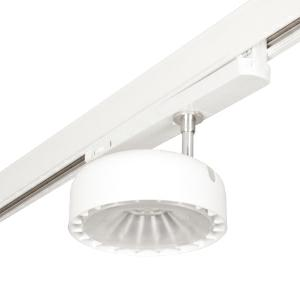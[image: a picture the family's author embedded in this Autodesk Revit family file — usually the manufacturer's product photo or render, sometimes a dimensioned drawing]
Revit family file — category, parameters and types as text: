
# Revit family: 3f_filippi_-_3f_emilio_track_ellittico_3f_filippi_-_47608_-_3f_emilio_tk_led_4000-840_ell
name_source: partatom
category: Lighting Fixtures
units: mm (PartAtom-declared; Revit-internal decimal feet)

## family parameters
Cut with Voids When Loaded = No
Host = Face
Light Source = No
Part Type = Normal
Room Calculation Point = No
Round Connector Dimension = Use Diameter
Shared = No

## types (1)
- 3F Filippi - 3F Emilio Track Ellittico (1 x LED, 4086 lm, 34 W, 4000 K)
    Apparent Load = 34 VA
    Approval mark = CE
    CIE Flux Codes = 84 95 99 100 100
    Color Rendering = 80
    Color Temperature = 4000 K
    Control Gear = Electronic ballast
    Default Elevation = 1800 mm
    Description = Adjustable spot light with minimal dimensions for accent lighting, to be integrated into the busbar.

ILLUMINOTECHNICAL
Luminous efficiency 100% (DLOR 100%, ULOR 0%).
Initial luminous flux of the luminaire 4086 lm.
Symmetrical and elliptical distribution.
Tabular UGR (CIE 117 - 4H-8H; S=0.25H; 70/50/20): RUG 22.5 - 27.
Beam angle: 46° - 89°.
Luminous efficacy 120 lm/W.
Lifetime (L90/B20): 30000 h. (tq+25°C)
Lifetime (L80/B20): 50000 h. (tq+25°C)
Sudden decreased luminous flux after 50000 hours: 0% (C0).
Photobiological safety in compliance with IEC/TR 62778: RG1 low risk, (IEC 62471).
In compliance with IEC/EN 62722-2-1 - IEC/EN 62717 standards.

SOURCE
Compact LED module 4000/840.
Energy efficiency class (UE 2019/2020 - UE 2019/2015): E.
CIE 13.3 Colour rendering index: CRI >80 (R9 <50%).
IES TM-30 Fidelity Index: Rf = 84 Rg = 95.
CCT nominal colour temperature 4000 K.
Colour initial tolerance (MacAdam): SDCM 3.
Zhaga Book 3 compliant.

MECHANICAL
Wired unit in white polycarbonate with busbar adaptor.
Single-piece in die-cast aluminium with passive dissipation, white colour, with perimeter cooling slots on upper edge, giving a crown of light effect to the fitting.
Invisible lock for positioning the luminous flux.
Lens made from transparent methacrylate (PMMA) with glossy surface and differentiated photo-etched.
Positioning arm in galvanised brass with sphere to allow for vertical positioning at angles from 0° to 90° and horizontal positioning from 0° to 290°.
Dimensions: diameter 130 mm, length 230 mm, height 105 mm. Weight 0.825 kg.
IP20 protection degree.
Glow-wire test resistance 650°C.

ELECTRICAL
Wiring unit separate from the body, invisible and integrated into the busbar.
Halogen Free electronic wiring 230V-50/60Hz, power factor 0.95, THD <25%, constant output current, SELV, class II, 1 driver.
Power of the luminaire 34 W.
ENEC - CE.
SAFE FLICKER: PstLM=<1 and SVM=<0.4 (IEC TR 61547-1 and IEC TR 63158), to ensure a more comfortable and safe light.
Ambient temperature from 0°C to +25°C.
Temperature class T6 max 85°C.
Relative humidity UR: <85%.

INSTALLATION
Track.

APPLICATIONS
Transit areas, spotlighting in commercial environments, exhibition areas, restaurants, shops and shop windows.

WARNING
Luminaire designed for disposal/recycling at end-of-life.
Replaceable (LED only) light source by a professional. Replaceable control gear by a professional.
    Height = 105 mm
    Lamp = 1 x LED
    Lamp Light Flux = 4086 lm
    Lamp Power = 34 W
    Lamp count = 1
    Length = 230 mm
    Lifetime = 50000 h
    Luminous efficacy = 120 lm/W
    Manufacturer = 3F Filippi
    ModVariant = No
    Model = 3F Filippi - 47608 - 3F Emilio TK LED 4000-840 ELL
    Mounting Place = Ceiling
    Mounting Type = Rail mounted
    Number of Poles = 1
    OnlyDefault = Yes
    Power Factor = 1
    Product Name = 3F Filippi - 3F Emilio Track Ellittico
    Product group = track mounted spotlight
    ProductGroupID = 12
    Protection Class = Protection class II
    Protection Degree = IP 20
    RLX_Detail_Level = 1
    RLX_Emergency_Light_Flux = 0 lm
    RLX_Emergency_Type = 0
    RLX_Emergency_Type_DB = No
    RlxData = <blob elided: 152661 chars, md5=f0919911>
    Socket = socket
    Standby Power = 0 W
    System Light Flux = 4086 lm
    System Power = 34 W
    Type Comments = Product without accessories
    Type Image = 3ffilippi_47608.jpg
    URL = http://relux.com
    VarID = ---
    Voltage = 0 V
    Weight = 0.00 kg
    Width = 130 mm

## geometry (parser evidence)
native form markers: Blend x4, Sweep x15
no freeform markers — native parametric forms only
